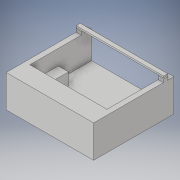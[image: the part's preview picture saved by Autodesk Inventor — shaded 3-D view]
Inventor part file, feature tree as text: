
AUTODESK INVENTOR PART (.ipt)
format: ipt  version: 2019 (Build 230136000, 136)  size: 182,784 bytes
history: native  units: mm
features: extrude x7, sketch x7
ambient origin geometry x8: Origin, YZ Plane, XZ Plane, XY Plane, X Axis, Y Axis, Z Axis, Center Point
bodies: Solid1 (feature_tree)
feature tree (14):
  extrude  "Extrusion1"  Depth=1460.0mm
  extrude  "Extrusion2"  Depth=200.0mm
  extrude  "Extrusion3"  Depth=200.0mm
  extrude  "Extrusion4"  Depth=235.0mm TaperAngle=0.0deg
  extrude  "Extrusion5"  Depth=100.0mm
  extrude  "Extrusion6"  Depth=100.0mm
  extrude  "Extrusion7"  Depth=260.0mm
  sketch  "Sketch1"  dims[d0=1500.0mm d1=1460.0mm]
  sketch  "Sketch2"  dims[d2=100.0mm d3=0.0mm d4=200.0mm]
  sketch  "Sketch3"  dims[d5=810.0mm d6=200.0mm]
  sketch  "Sketch4"  dims[d7=810.0mm d8=235.0mm d9=0.0mm]
  sketch  "Sketch5"  dims[d10=100.0mm d11=100.0mm]
  sketch  "Sketch6"  dims[d12=1700.0mm d13=100.0mm]
  sketch  "Sketch7"  dims[d14=630.0mm d15=0.0mm d16=260.0mm d17=60.0mm d18=1500.0mm d19=0.0mm d20=120.0mm d21=120.0mm d22=80.0mm d23=80.0mm d24=110.0mm d25=0.0mm d26=30.0mm d27=1700.0mm d28=20.0mm d29=80.0mm d30=0.0mm d31=80.0mm d32=30.0mm d33=1500.0mm d34=0.0mm]
